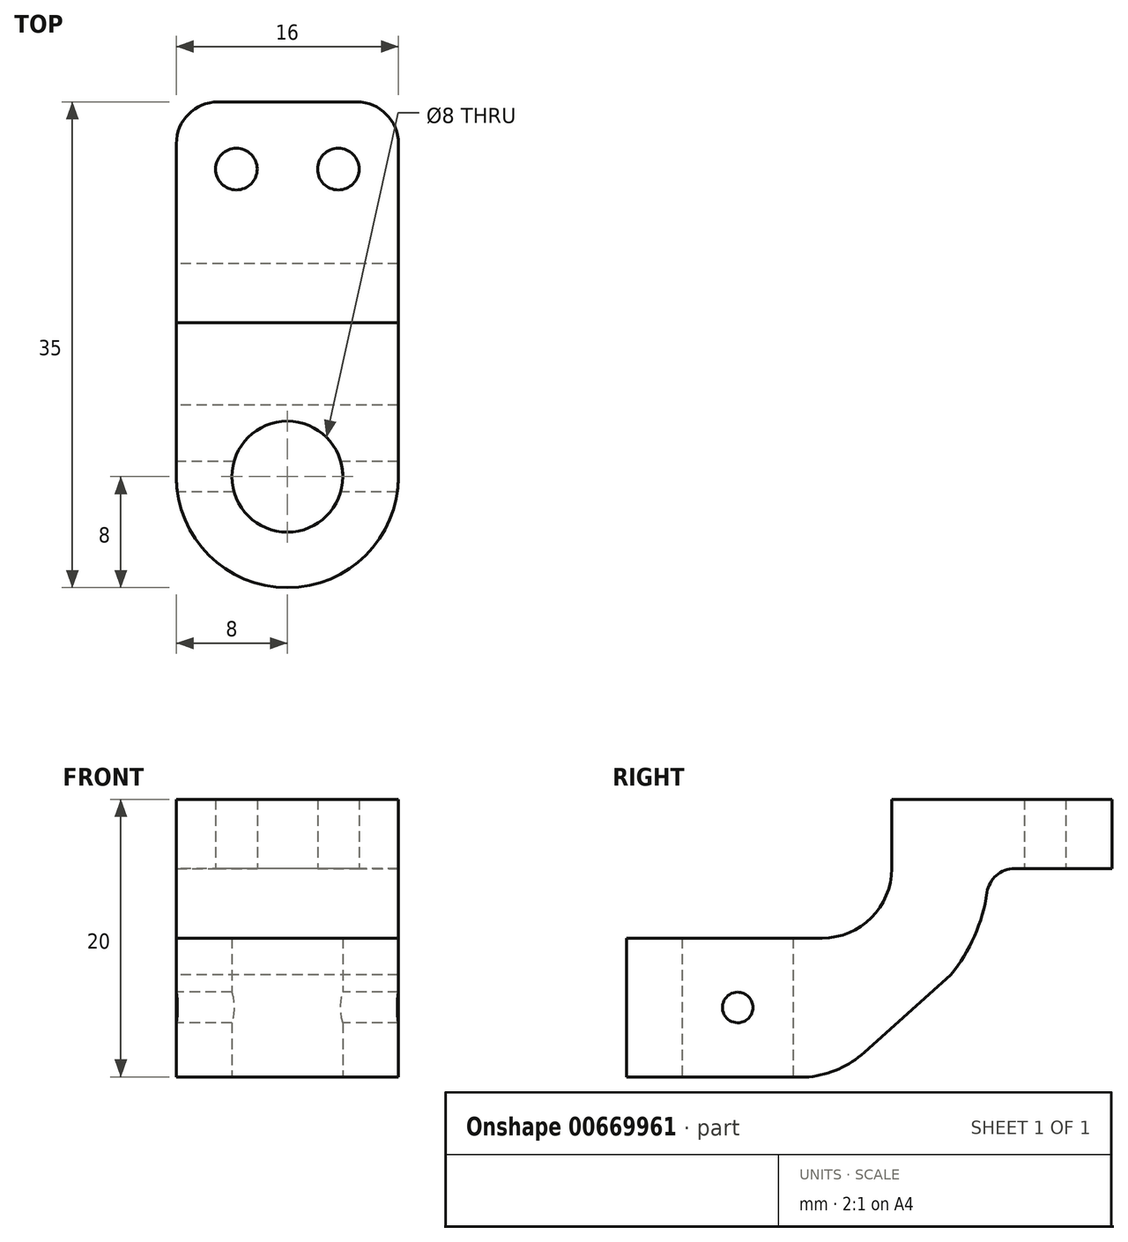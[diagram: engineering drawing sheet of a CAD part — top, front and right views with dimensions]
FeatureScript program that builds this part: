
annotation { "Feature Type Name" : "Feature", "Feature Type Description" : "" }
export const myFeature = defineFeature(function(context is Context, id is Id, definition is map)
    precondition{}
    {
        {
            var Q0;
            Q0=qCreatedBy(makeId("Top.planeOp"),FACE);
            var sketch = newSketch(context, id + "F0", { "sketchPlane" : qUnion([Q0])});
            skCircle(sketch, "E0", {"center": v(0, 0) * mm, "radius": 4 * mm});
            skArc(sketch, "E1", {"start": v(8, 0) * mm, "mid": v(0, -8) * mm, "end": v(-8, 0) * mm});
            skLineSegment(sketch, "E2", {"start": v(-8, 0) * mm, "end": v(-8, 24) * mm});
            skLineSegment(sketch, "E3", {"start": v(-5, 27) * mm, "end": v(5, 27) * mm});
            skLineSegment(sketch, "E4", {"start": v(8, 24) * mm, "end": v(8, 0) * mm});
            skCircle(sketch, "E5", {"center": v(-3.68, 22.16) * mm, "radius": 1.5 * mm});
            skCircle(sketch, "E6", {"center": v(3.68, 22.16) * mm, "radius": 1.5 * mm});
            skPoint(sketch, "E7.visualSharp", {"position": v(8, 27) * mm});
            skArc(sketch, "E7.filletArc", {"start": v(8, 24) * mm, "mid": v(7.12, 26.12) * mm, "end": v(5, 27) * mm});
            skPoint(sketch, "E8.visualSharp", {"position": v(-8, 27) * mm});
            skArc(sketch, "E8.filletArc", {"start": v(-5, 27) * mm, "mid": v(-7.12, 26.12) * mm, "end": v(-8, 24) * mm});
            skSolve(sketch);
        }
        {
            var Q0;
            Q0=makeQuery(id+"F0.imprint","IMPRINT",FACE,{"disambiguationData":[TD([[makeQuery(id+"F0.imprint","IMPRINT",EDGE,{"derivedFrom":sQuery(id+"F0.wireOp",EDGE,"E0")}),-1.0]])]});
            extrude(context, id + "F1", {"entities" : qUnion([Q0]), "depth" : 20 * mm, "offsetDistance" : 25 * mm});
        }
        {
            var Q0;
            Q0=qCreatedBy(makeId("Front.planeOp"),FACE);
            var sketch = newSketch(context, id + "F2", { "sketchPlane" : qUnion([Q0])});
            skLineSegment(sketch, "E9.bottom", {"start": v(-18, 29.2) * mm, "end": v(17.65, 29.2) * mm});
            skLineSegment(sketch, "E9.top", {"start": v(-18, 10) * mm, "end": v(17.65, 10) * mm});
            skLineSegment(sketch, "E9.left", {"start": v(-18, 29.2) * mm, "end": v(-18, 10) * mm});
            skLineSegment(sketch, "E9.right", {"start": v(17.65, 29.2) * mm, "end": v(17.65, 10) * mm});
            skSolve(sketch);
        }
        {
            var Q0;
            Q0=makeQuery(id+"F1.opExtrude","SWEPT_FACE",FACE,{"disambiguationData":[OSD([sQuery(id+"F0.wireOp",EDGE,"E2")])]});
            var sketch = newSketch(context, id + "F3", { "sketchPlane" : qUnion([Q0])});
            skLineSegment(sketch, "E10", {"start": v(-11.1, 34.12) * mm, "end": v(-11.1, 15) * mm});
            skLineSegment(sketch, "E11", {"start": v(15.47, 10) * mm, "end": v(-6.1, 10) * mm});
            skLineSegment(sketch, "E12", {"start": v(-11.1, 34.12) * mm, "end": v(15.48, 34.12) * mm});
            skLineSegment(sketch, "E13", {"start": v(15.48, 34.12) * mm, "end": v(15.47, 10) * mm});
            skPoint(sketch, "E14.visualSharp", {"position": v(-11.1, 10) * mm});
            skArc(sketch, "E14.filletArc", {"start": v(-11.1, 15) * mm, "mid": v(-9.64, 11.46) * mm, "end": v(-6.1, 10) * mm});
            skLineSegment(sketch, "E15", {"start": v(-48.32, 15) * mm, "end": v(-19.96, 15) * mm});
            skLineSegment(sketch, "E16", {"start": v(-48.32, 15) * mm, "end": v(-48.32, 0) * mm});
            skArc(sketch, "E17", {"start": v(-17.98, 13.29) * mm, "mid": v(-17.08, 10.14) * mm, "end": v(-15.36, 7.36) * mm});
            skPoint(sketch, "E18.visualSharp", {"position": v(-18.1, 15) * mm});
            skArc(sketch, "E18.filletArc", {"start": v(-17.98, 13.29) * mm, "mid": v(-18.65, 14.51) * mm, "end": v(-19.96, 15) * mm});
            skLineSegment(sketch, "E19", {"start": v(-5.15, 0) * mm, "end": v(-5.15, -8.18) * mm});
            skLineSegment(sketch, "E20", {"start": v(-5.15, -8.18) * mm, "end": v(-48.32, -8.18) * mm});
            skLineSegment(sketch, "E21", {"start": v(-48.32, 0) * mm, "end": v(-48.32, -8.18) * mm});
            skLineSegment(sketch, "E22", {"start": v(-15.36, 7.36) * mm, "end": v(-9.14, 1.76) * mm});
            skArc(sketch, "E23", {"start": v(-9.14, 1.76) * mm, "mid": v(-7.29, 0.56) * mm, "end": v(-5.15, 0) * mm});
            skLineSegment(sketch, "E24", {"start": v(36.05, 5) * mm, "end": v(-113.45, 5) * mm, "construction": true});
            skCircle(sketch, "E25", {"center": v(0, 5) * mm, "radius": 1.1 * mm});
            skSolve(sketch);
        }
        {
            var Q0;
            Q0 = qSketchRegion(id + "F3", true);
            extrude(context, id + "F4", {"entities" : qUnion([Q0]), "operationType" : NewBodyOperationType.REMOVE, "endBound" : BoundingType.THROUGH_ALL, "oppositeDirection" : true, "depth" : 25 * mm, "offsetDistance" : 25 * mm});
        }
    });
